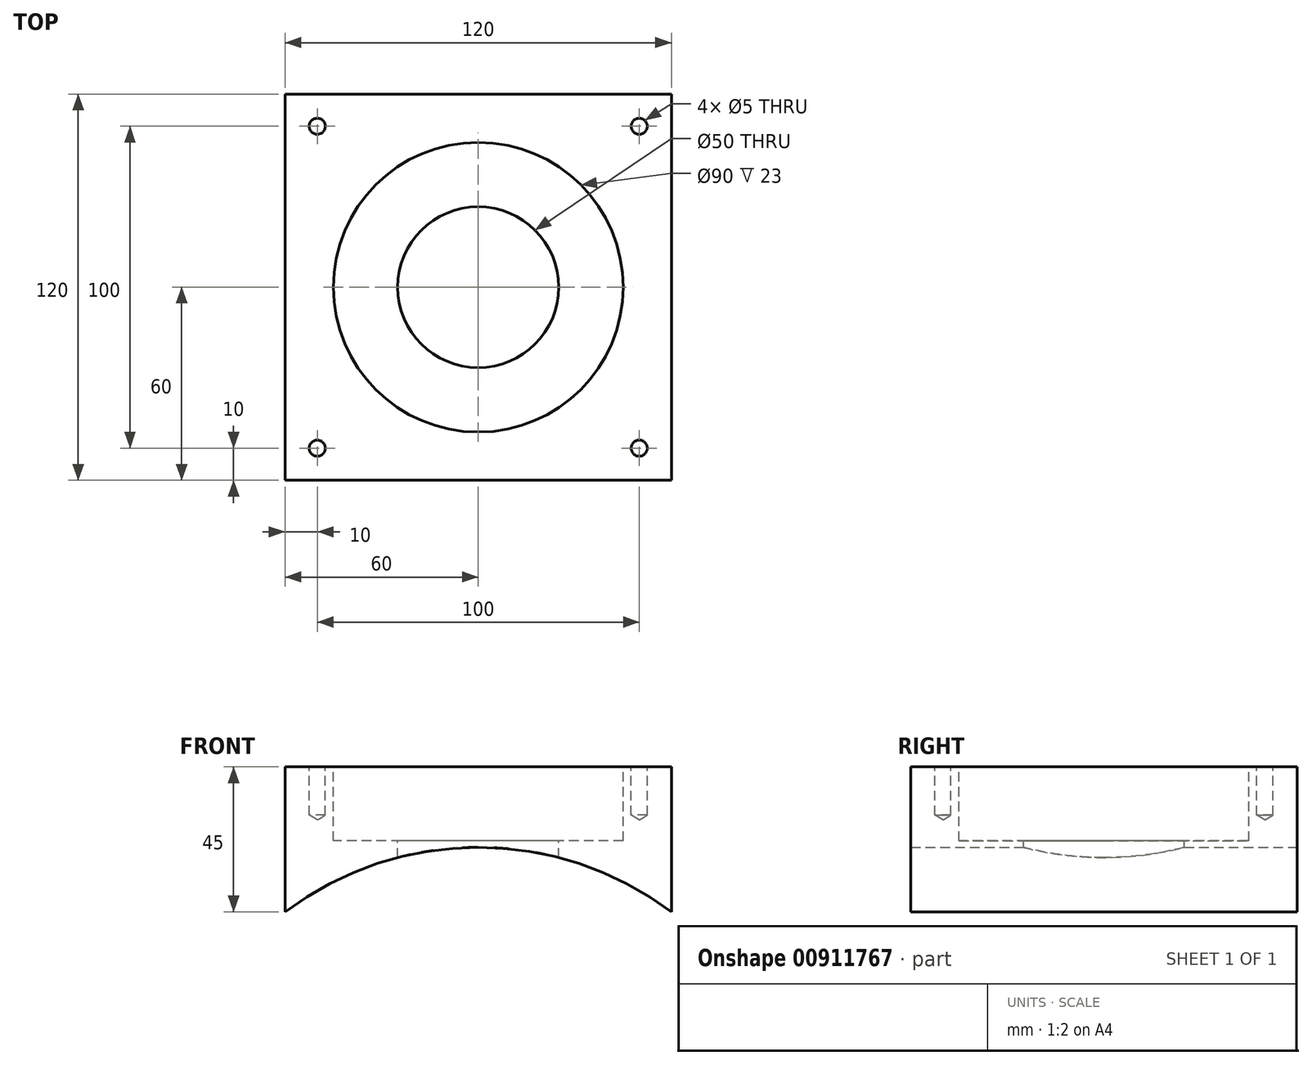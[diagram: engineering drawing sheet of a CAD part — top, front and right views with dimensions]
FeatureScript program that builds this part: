
annotation { "Feature Type Name" : "Feature", "Feature Type Description" : "" }
export const myFeature = defineFeature(function(context is Context, id is Id, definition is map)
    precondition{}
    {
        {
            var Q0;
            Q0=qCreatedBy(makeId("Front.planeOp"),FACE);
            var sketch = newSketch(context, id + "F0", { "sketchPlane" : qUnion([Q0])});
            skCircle(sketch, "E0", {"center": v(0, 0) * mm, "radius": 100 * mm});
            skLineSegment(sketch, "E1", {"start": v(0, 0) * mm, "end": v(0, 100) * mm});
            skLineSegment(sketch, "E2.bottom", {"start": v(60, 75) * mm, "end": v(-60, 75) * mm});
            skLineSegment(sketch, "E2.top", {"start": v(60, 125) * mm, "end": v(-60, 125) * mm});
            skLineSegment(sketch, "E2.left", {"start": v(60, 75) * mm, "end": v(60, 125) * mm});
            skLineSegment(sketch, "E2.right", {"start": v(-60, 75) * mm, "end": v(-60, 125) * mm});
            skPoint(sketch, "E2.middle", {"position": v(0, 100) * mm});
            skSolve(sketch);
        }
        {
            var Q0;
            {var subQ1=sQuery(id+"F0.wireOp",EDGE,"E2.top");Q0=makeQuery(id+"F0.imprint","IMPRINT",FACE,{"disambiguationData":[TD([[makeQuery(id+"F0.imprint","IMPRINT",EDGE,{"derivedFrom":subQ1}),1.0]])]});}
            extrude(context, id + "F1", {"entities" : qUnion([Q0]), "depth" : 120 * mm, "offsetDistance" : 25 * mm, "symmetric" : true});
        }
        {
            var Q0;
            Q0=makeQuery(id+"F1.opExtrude","SWEPT_FACE",FACE,{"disambiguationData":[OSD([sQuery(id+"F0.wireOp",EDGE,"E2.top")])]});
            var sketch = newSketch(context, id + "F2", { "sketchPlane" : qUnion([Q0])});
            skCircle(sketch, "E3", {"center": v(0, 0) * mm, "radius": 25 * mm});
            skSolve(sketch);
        }
        {
            var Q0;
            Q0=qSketchRegion(id+"F2",true);
            extrude(context, id + "F3", {"entities" : qUnion([Q0]), "operationType" : NewBodyOperationType.REMOVE, "oppositeDirection" : true, "depth" : 50 * mm, "offsetDistance" : 25 * mm});
        }
        {
            var Q0;
            Q0=makeQuery(id+"F1.opExtrude","SWEPT_FACE",FACE,{"disambiguationData":[OSD([sQuery(id+"F0.wireOp",EDGE,"E2.top")])]});
            var sketch = newSketch(context, id + "F4", { "sketchPlane" : qUnion([Q0])});
            skCircle(sketch, "E4", {"center": v(0, 0) * mm, "radius": 45 * mm});
            skSolve(sketch);
        }
        {
            var Q0;
            Q0=qSketchRegion(id+"F4",true);
            extrude(context, id + "F5", {"entities" : qUnion([Q0]), "operationType" : NewBodyOperationType.REMOVE, "oppositeDirection" : true, "depth" : 23 * mm, "offsetDistance" : 25 * mm});
        }
        {
            var Q0;
            Q0=makeQuery(id+"F1.opExtrude","SWEPT_FACE",FACE,{"disambiguationData":[OSD([sQuery(id+"F0.wireOp",EDGE,"E2.top")])]});
            var sketch = newSketch(context, id + "F6", { "sketchPlane" : qUnion([Q0])});
            skPoint(sketch, "E5", {"position": v(-50, 50) * mm});
            skPoint(sketch, "E6", {"position": v(50, 50) * mm});
            skPoint(sketch, "E7", {"position": v(-50, -50) * mm});
            skPoint(sketch, "E8", {"position": v(50, -50) * mm});
            skSolve(sketch);
        }
        {
            var Q0;
            Q0=sQuery(id+"F6.wireOp",VERTEX,"E5");
            var Q1;
            Q1=sQuery(id+"F6.wireOp",VERTEX,"E6");
            var Q2;
            Q2=sQuery(id+"F6.wireOp",VERTEX,"E8");
            var Q3;
            Q3=sQuery(id+"F6.wireOp",VERTEX,"E7");
            var Q4;
            Q4=makeQuery(id+"F1.opExtrude","SWEPT_BODY",BODY,{"disambiguationData":[OSD([sQuery(id+"F0.wireOp",EDGE,"E0"),sQuery(id+"F0.wireOp",EDGE,"E2.top"),sQuery(id+"F0.wireOp",EDGE,"E2.left"),sQuery(id+"F0.wireOp",EDGE,"E2.right")])]});
            hole(context, id + "F7", {"style" : HoleStyle.SIMPLE, "endStyle" : HoleEndStyle.BLIND, "standardTappedOrClearance" : lookupTablePath({ "standard" : "ISO", "engagement" : "75%", "pitch" : "1 mm", "size" : "M6", "type" : "Tapped" }), "standardBlindInLast" : lookupTablePath({ "standard" : "ISO", "engagement" : "75%", "pitch" : "1 mm", "size" : "M6", "type" : "Tapped" }), "holeDiameter" : 5 * mm, "majorDiameter" : 6 * mm, "showTappedDepth" : true, "holeDepth" : 15 * mm, "isTappedThrough" : true, "tappedDepth" : 12 * mm, "tapClearance" : 3, "startFromSketch" : true, "locations" : qUnion([Q0, Q1, Q2, Q3]), "scope" : qUnion([Q4])});
        }
    });
